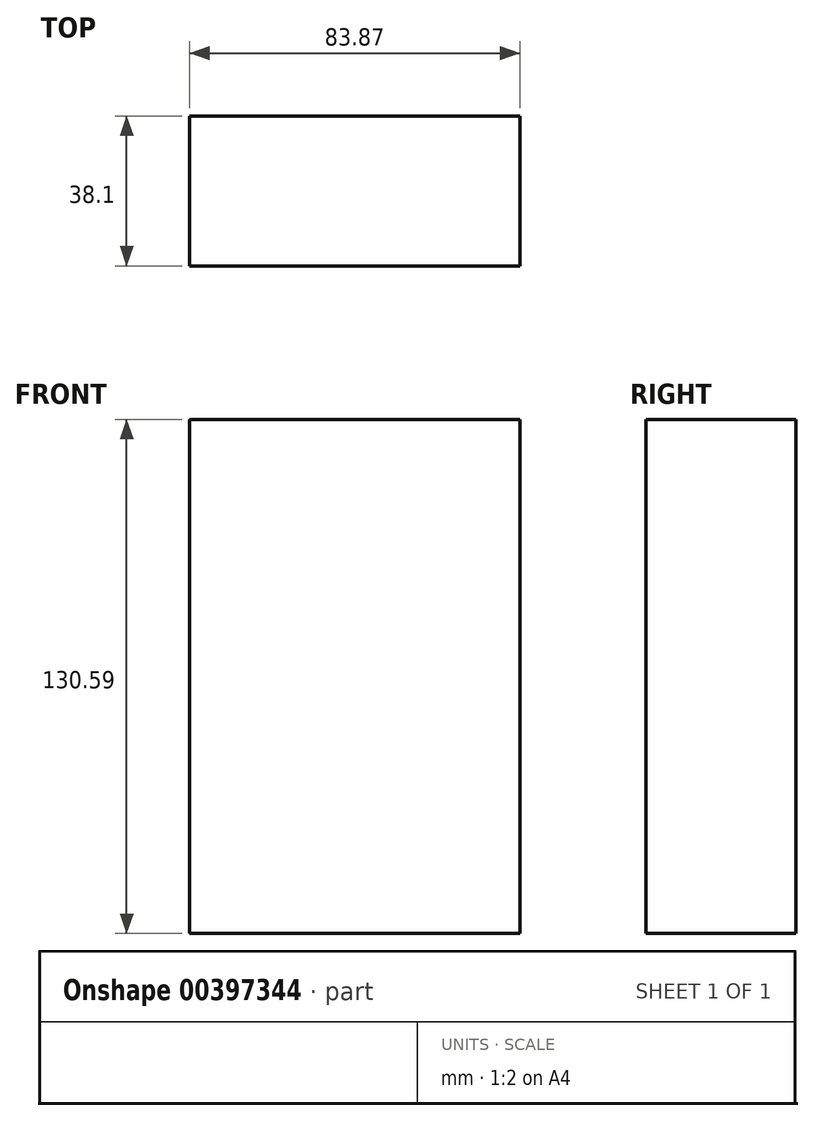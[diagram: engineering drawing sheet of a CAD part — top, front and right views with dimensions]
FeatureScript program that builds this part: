
annotation { "Feature Type Name" : "Feature", "Feature Type Description" : "" }
export const myFeature = defineFeature(function(context is Context, id is Id, definition is map)
    precondition{}
    {
        {
            var Q0;
            Q0=qCreatedBy(makeId("Front.planeOp"),FACE);
            var sketch = newSketch(context, id + "F0", { "sketchPlane" : qUnion([Q0])});
            skLineSegment(sketch, "E0.bottom", {"start": v(-66.58, -55.18) * mm, "end": v(17.29, -55.18) * mm});
            skLineSegment(sketch, "E0.top", {"start": v(-66.58, 75.41) * mm, "end": v(17.29, 75.41) * mm});
            skLineSegment(sketch, "E0.left", {"start": v(-66.58, -55.18) * mm, "end": v(-66.58, 75.41) * mm});
            skLineSegment(sketch, "E0.right", {"start": v(17.29, -55.18) * mm, "end": v(17.29, 75.41) * mm});
            skSolve(sketch);
        }
        {
            var Q0;
            Q0=makeQuery(id+"F0.imprint","IMPRINT",FACE,{"disambiguationData":[TD([[makeQuery(id+"F0.imprint","IMPRINT",EDGE,{"derivedFrom":sQuery(id+"F0.wireOp",EDGE,"E0.bottom")}),1.0]])]});
            extrude(context, id + "F1", {"entities" : qUnion([Q0]), "depth" : 38.1 * mm});
        }
    });
